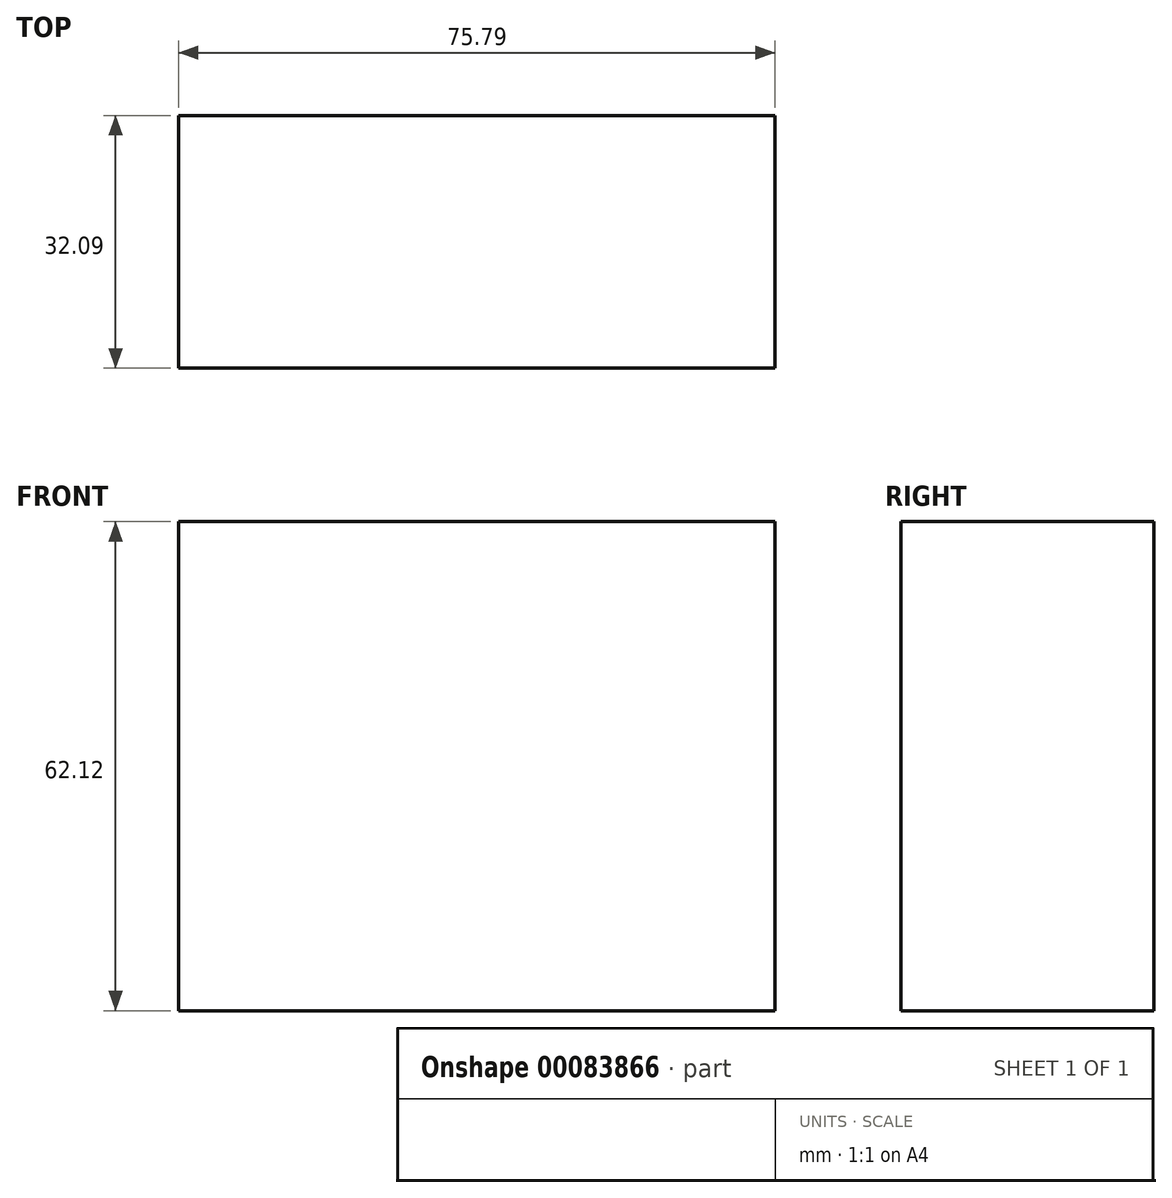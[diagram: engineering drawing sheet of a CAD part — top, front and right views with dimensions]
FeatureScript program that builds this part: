
annotation { "Feature Type Name" : "Feature", "Feature Type Description" : "" }
export const myFeature = defineFeature(function(context is Context, id is Id, definition is map)
    precondition{}
    {
        {
            var Q0;
            Q0=qCreatedBy(makeId("Top.planeOp"),FACE);
            var sketch = newSketch(context, id + "F0", { "sketchPlane" : qUnion([Q0])});
            skLineSegment(sketch, "E0.bottom", {"start": v(-175.85, 48.62) * mm, "end": v(-100.06, 48.62) * mm});
            skLineSegment(sketch, "E0.top", {"start": v(-175.85, 16.53) * mm, "end": v(-100.06, 16.53) * mm});
            skLineSegment(sketch, "E0.left", {"start": v(-175.85, 48.62) * mm, "end": v(-175.85, 16.53) * mm});
            skLineSegment(sketch, "E0.right", {"start": v(-100.06, 48.62) * mm, "end": v(-100.06, 16.53) * mm});
            skSolve(sketch);
        }
        {
            var Q0;
            Q0=makeQuery(id+"F0.imprint","IMPRINT",FACE,{"disambiguationData":[TD([[makeQuery(id+"F0.imprint","IMPRINT",EDGE,{"derivedFrom":sQuery(id+"F0.wireOp",EDGE,"E0.bottom")}),-1.0]])]});
            extrude(context, id + "F1", {"entities" : qUnion([Q0]), "depth" : 62.12 * mm});
        }
    });
